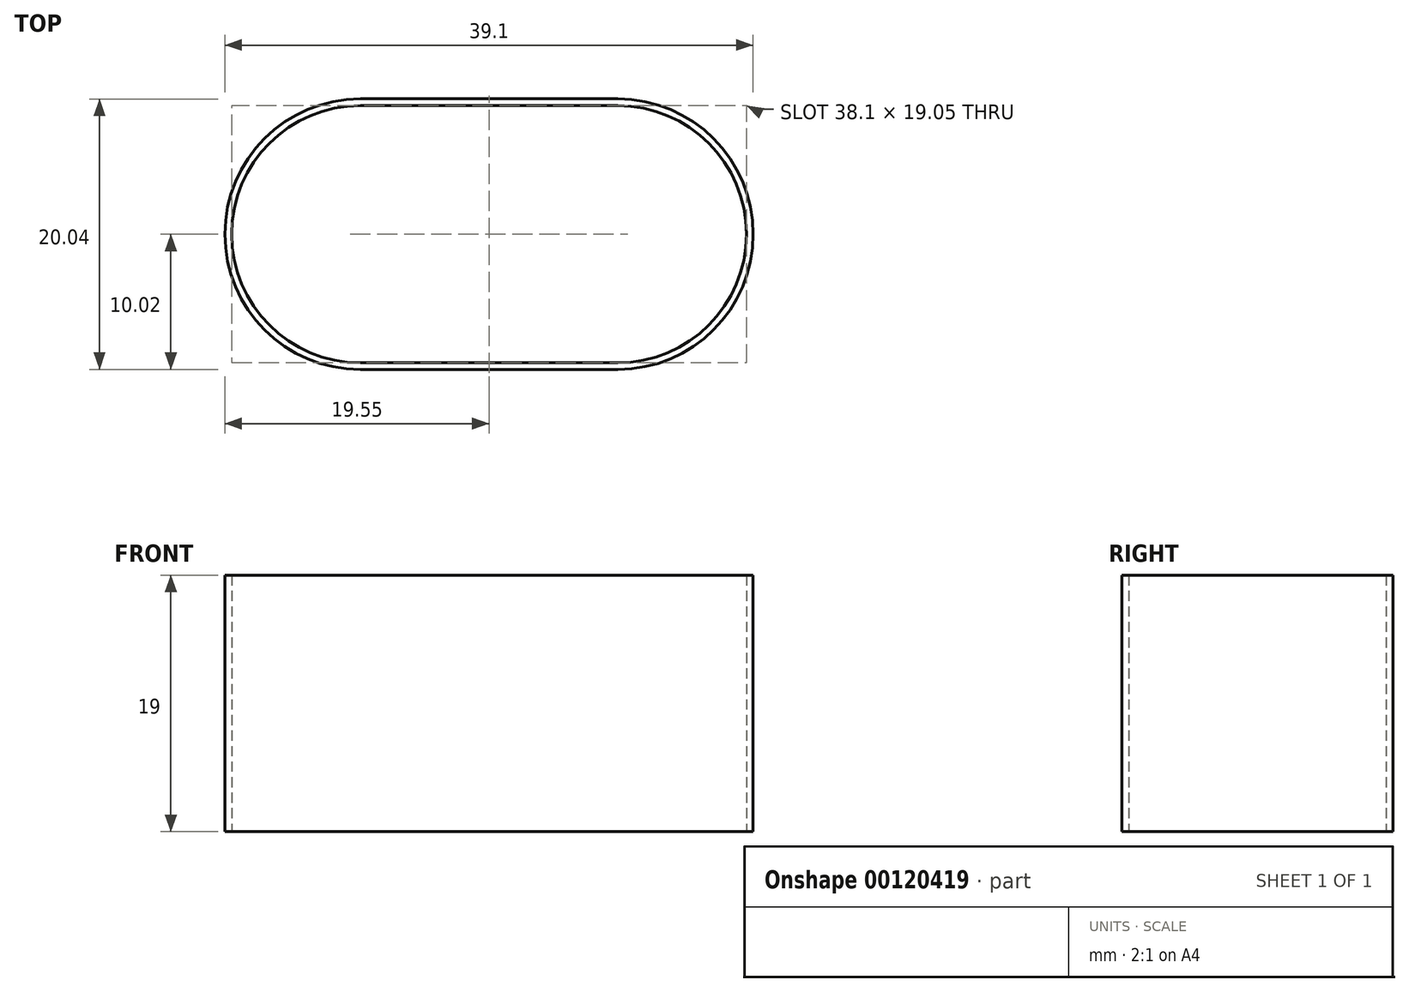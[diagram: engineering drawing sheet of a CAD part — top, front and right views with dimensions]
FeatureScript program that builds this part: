
annotation { "Feature Type Name" : "Feature", "Feature Type Description" : "" }
export const myFeature = defineFeature(function(context is Context, id is Id, definition is map)
    precondition{}
    {
        {
            var Q0;
            Q0=qCreatedBy(makeId("Top.planeOp"),FACE);
            var sketch = newSketch(context, id + "F0", { "sketchPlane" : qUnion([Q0])});
            skLineSegment(sketch, "E0", {"start": v(-9.53, 0) * mm, "end": v(9.53, 0) * mm, "construction": true});
            skArc(sketch, "E1.0.startCap", {"start": v(-9.53, -9.53) * mm, "mid": v(-19.05, 0) * mm, "end": v(-9.53, 9.52) * mm});
            skArc(sketch, "E1.0.endCap", {"start": v(9.53, 9.53) * mm, "mid": v(19.05, 0) * mm, "end": v(9.53, -9.53) * mm});
            skLineSegment(sketch, "E1.0.left", {"start": v(-9.53, 9.53) * mm, "end": v(9.53, 9.53) * mm});
            skLineSegment(sketch, "E1.0.right", {"start": v(-9.53, -9.53) * mm, "end": v(9.53, -9.53) * mm});
            skLineSegment(sketch, "E2", {"start": v(-19.05, 0) * mm, "end": v(19.05, 0) * mm, "construction": true});
            skLineSegment(sketch, "E3.0", {"start": v(-9.52, -10.03) * mm, "end": v(9.53, -10.03) * mm});
            skArc(sketch, "E3.1", {"start": v(-9.52, -10.03) * mm, "mid": v(-19.55, 0) * mm, "end": v(-9.53, 10.03) * mm});
            skLineSegment(sketch, "E3.2", {"start": v(-9.53, 10.03) * mm, "end": v(9.52, 10.03) * mm});
            skArc(sketch, "E3.3", {"start": v(9.52, 10.03) * mm, "mid": v(19.55, 0) * mm, "end": v(9.53, -10.03) * mm});
            skSolve(sketch);
        }
        {
            var Q0;
            Q0=makeQuery(id+"F0.imprint","IMPRINT",FACE,{"disambiguationData":[TD([[makeQuery(id+"F0.imprint","IMPRINT",EDGE,{"derivedFrom":sQuery(id+"F0.wireOp",EDGE,"E1.0.startCap")}),-1.0]])]});
            extrude(context, id + "F1", {"entities" : qUnion([Q0]), "depth" : 19 * mm});
        }
    });
